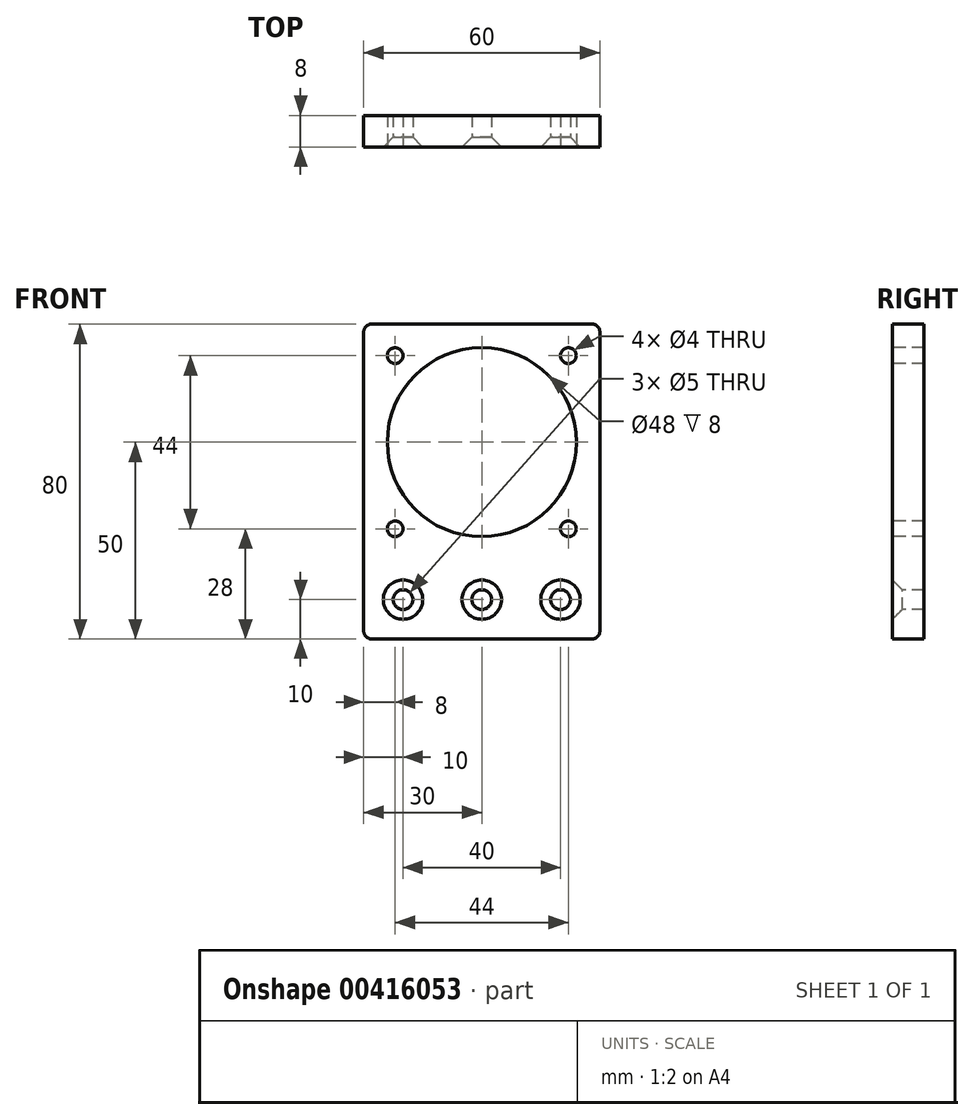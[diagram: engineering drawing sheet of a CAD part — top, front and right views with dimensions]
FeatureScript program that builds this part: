
annotation { "Feature Type Name" : "Feature", "Feature Type Description" : "" }
export const myFeature = defineFeature(function(context is Context, id is Id, definition is map)
    precondition{}
    {
        {
            var Q0;
            Q0=qCreatedBy(makeId("Front.planeOp"),FACE);
            var sketch = newSketch(context, id + "F0", { "sketchPlane" : qUnion([Q0])});
            skLineSegment(sketch, "E0.bottom", {"start": v(2, 0) * mm, "end": v(58, 0) * mm});
            skLineSegment(sketch, "E0.top", {"start": v(2, 80) * mm, "end": v(58, 80) * mm});
            skLineSegment(sketch, "E0.left", {"start": v(0, 2) * mm, "end": v(0, 78) * mm});
            skLineSegment(sketch, "E0.right", {"start": v(60, 2) * mm, "end": v(60, 78) * mm});
            skCircle(sketch, "E1", {"center": v(30, 50) * mm, "radius": 24 * mm});
            skPoint(sketch, "E2", {"position": v(30, 80) * mm});
            skPoint(sketch, "E3", {"position": v(10, 10) * mm});
            skPoint(sketch, "E4", {"position": v(30, 10) * mm});
            skPoint(sketch, "E5", {"position": v(50, 10) * mm});
            skPoint(sketch, "E6.visualSharp", {"position": v(0, 80) * mm});
            skArc(sketch, "E6.filletArc", {"start": v(2, 80) * mm, "mid": v(0.59, 79.41) * mm, "end": v(0, 78) * mm});
            skPoint(sketch, "E7.visualSharp", {"position": v(60, 80) * mm});
            skArc(sketch, "E7.filletArc", {"start": v(60, 78) * mm, "mid": v(59.41, 79.41) * mm, "end": v(58, 80) * mm});
            skPoint(sketch, "E8.visualSharp", {"position": v(60, 0) * mm});
            skArc(sketch, "E8.filletArc", {"start": v(58, 0) * mm, "mid": v(59.41, 0.59) * mm, "end": v(60, 2) * mm});
            skPoint(sketch, "E9.visualSharp", {"position": v(0, 0) * mm});
            skArc(sketch, "E9.filletArc", {"start": v(0, 2) * mm, "mid": v(0.59, 0.59) * mm, "end": v(2, 0) * mm});
            skPoint(sketch, "E10", {"position": v(8, 72) * mm});
            skPoint(sketch, "E11", {"position": v(52, 72) * mm});
            skPoint(sketch, "E12", {"position": v(52, 28) * mm});
            skPoint(sketch, "E13", {"position": v(8, 28) * mm});
            skLineSegment(sketch, "E14", {"start": v(8, 72) * mm, "end": v(30, 50) * mm, "construction": true});
            skSolve(sketch);
        }
        {
            var Q0;
            Q0 = qSketchRegion(id + "F0", true);
            extrude(context, id + "F1", {"entities" : qUnion([Q0]), "depth" : -8 * mm});
        }
        {
            var Q0;
            Q0=sQuery(id+"F0.wireOp",VERTEX,"E3");
            var Q1;
            Q1=sQuery(id+"F0.wireOp",VERTEX,"E4");
            var Q2;
            Q2=sQuery(id+"F0.wireOp",VERTEX,"E5");
            var Q3;
            Q3=makeQuery(id+"F1.opExtrude","SWEPT_BODY",BODY,{"disambiguationData":[OSD([sQuery(id+"F0.wireOp",EDGE,"E0.bottom"),sQuery(id+"F0.wireOp",EDGE,"E0.top"),sQuery(id+"F0.wireOp",EDGE,"E0.left"),sQuery(id+"F0.wireOp",EDGE,"E0.right"),sQuery(id+"F0.wireOp",EDGE,"E1"),sQuery(id+"F0.wireOp",EDGE,"E6.filletArc"),sQuery(id+"F0.wireOp",EDGE,"E7.filletArc"),sQuery(id+"F0.wireOp",EDGE,"E8.filletArc"),sQuery(id+"F0.wireOp",EDGE,"E9.filletArc")])]});
            hole(context, id + "F2", {"style" : HoleStyle.C_SINK, "endStyle" : HoleEndStyle.THROUGH, "holeDiameter" : 5 * mm, "cSinkDiameter" : 10 * mm, "cSinkAngle" : 90 * degree, "tappedDepth" : 12 * mm, "tapClearance" : 3, "locations" : qUnion([Q0, Q1, Q2]), "scope" : qUnion([Q3])});
        }
        {
            var Q0;
            Q0=sQuery(id+"F0.wireOp",VERTEX,"E10");
            var Q1;
            Q1=sQuery(id+"F0.wireOp",VERTEX,"E11");
            var Q2;
            Q2=sQuery(id+"F0.wireOp",VERTEX,"E12");
            var Q3;
            Q3=sQuery(id+"F0.wireOp",VERTEX,"E13");
            var Q4;
            Q4=makeQuery(id+"F1.opExtrude","SWEPT_BODY",BODY,{"disambiguationData":[OSD([sQuery(id+"F0.wireOp",EDGE,"E0.bottom"),sQuery(id+"F0.wireOp",EDGE,"E0.top"),sQuery(id+"F0.wireOp",EDGE,"E0.left"),sQuery(id+"F0.wireOp",EDGE,"E0.right"),sQuery(id+"F0.wireOp",EDGE,"E1"),sQuery(id+"F0.wireOp",EDGE,"E6.filletArc"),sQuery(id+"F0.wireOp",EDGE,"E7.filletArc"),sQuery(id+"F0.wireOp",EDGE,"E8.filletArc"),sQuery(id+"F0.wireOp",EDGE,"E9.filletArc")])]});
            hole(context, id + "F3", {"style" : HoleStyle.SIMPLE, "endStyle" : HoleEndStyle.THROUGH, "holeDiameter" : 4 * mm, "tappedDepth" : 12 * mm, "tapClearance" : 3, "locations" : qUnion([Q0, Q1, Q2, Q3]), "scope" : qUnion([Q4])});
        }
    });
